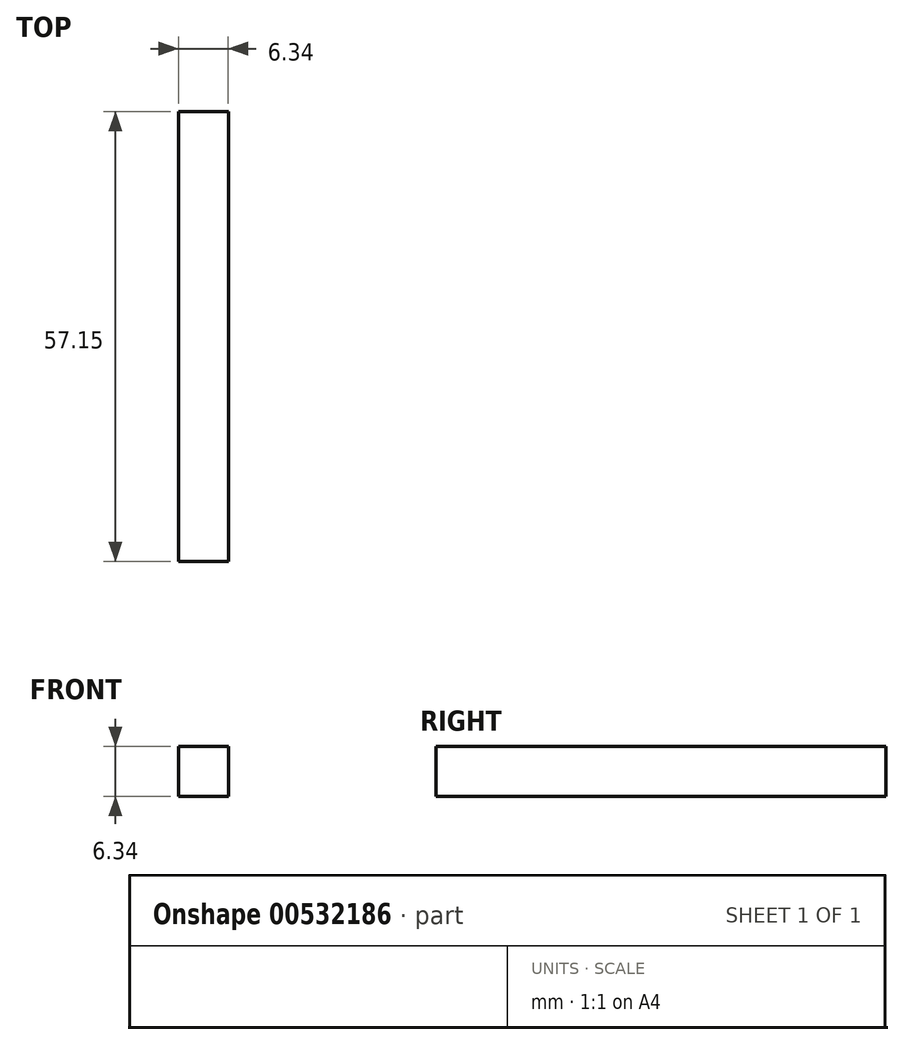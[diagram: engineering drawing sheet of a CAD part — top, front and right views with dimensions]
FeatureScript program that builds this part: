
annotation { "Feature Type Name" : "Feature", "Feature Type Description" : "" }
export const myFeature = defineFeature(function(context is Context, id is Id, definition is map)
    precondition{}
    {
        {
            var Q0;
            Q0=qCreatedBy(makeId("Front.planeOp"),FACE);
            var sketch = newSketch(context, id + "F0", { "sketchPlane" : qUnion([Q0])});
            skLineSegment(sketch, "E0.bottom", {"start": v(3.18, 3.18) * mm, "end": v(-3.18, 3.18) * mm});
            skLineSegment(sketch, "E0.top", {"start": v(3.18, -3.17) * mm, "end": v(-3.18, -3.17) * mm});
            skLineSegment(sketch, "E0.left", {"start": v(3.18, 3.18) * mm, "end": v(3.18, -3.18) * mm});
            skLineSegment(sketch, "E0.right", {"start": v(-3.18, 3.18) * mm, "end": v(-3.18, -3.17) * mm});
            skPoint(sketch, "E0.middle", {"position": v(0, 0) * mm});
            skSolve(sketch);
        }
        {
            var Q0;
            Q0 = qSketchRegion(id + "F0", true);
            extrude(context, id + "F1", {"entities" : qUnion([Q0]), "depth" : 25.4 * mm, "offsetDistance" : 25.4 * mm, "hasSecondDirection" : true, "secondDirectionOppositeDirection" : true, "secondDirectionDepth" : 31.75 * mm});
        }
    });
